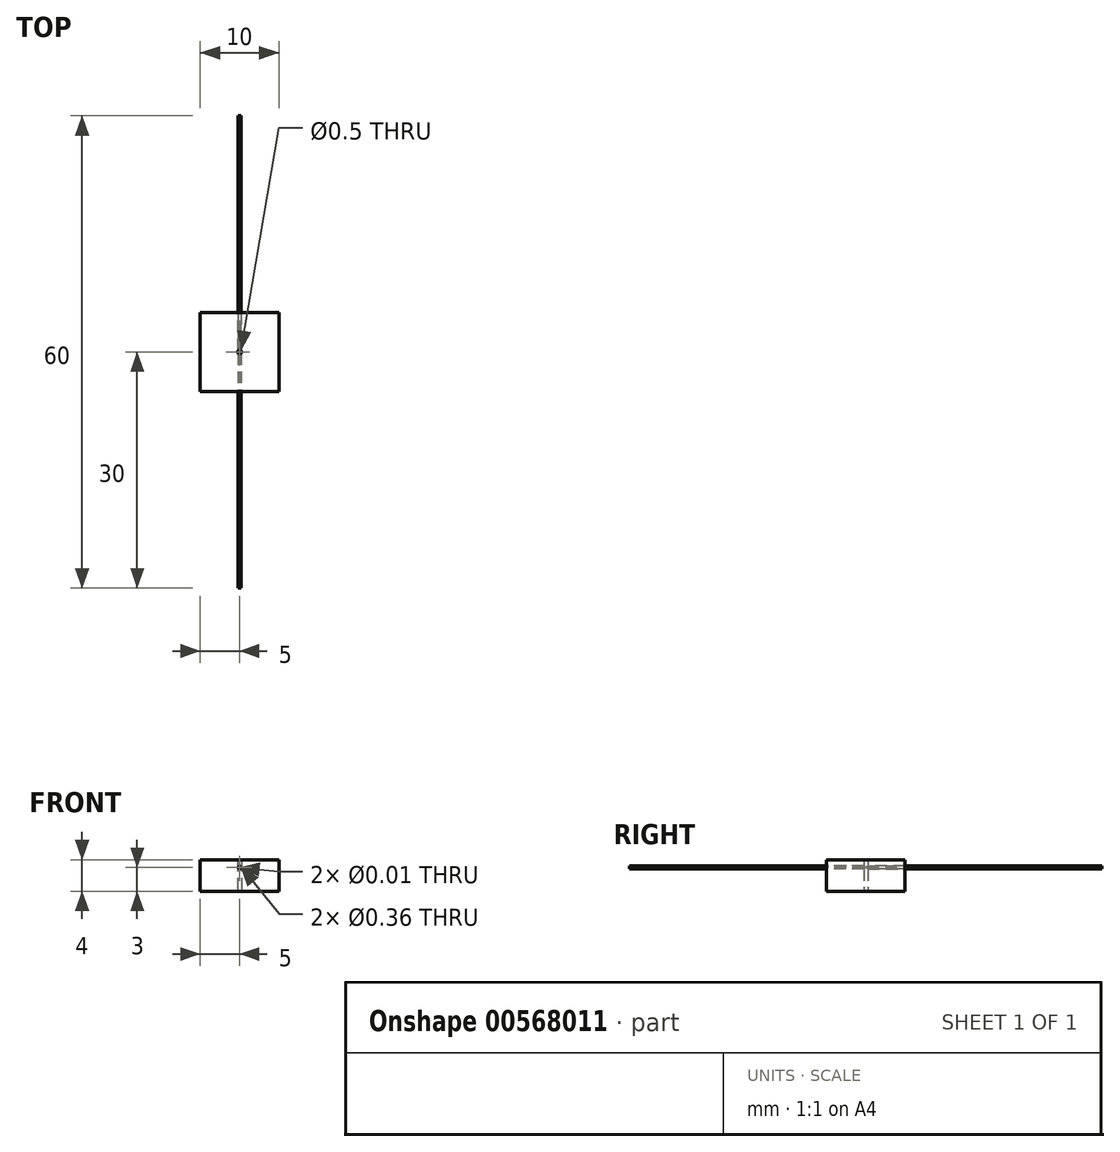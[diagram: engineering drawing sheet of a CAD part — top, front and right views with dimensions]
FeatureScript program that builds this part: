
annotation { "Feature Type Name" : "Feature", "Feature Type Description" : "" }
export const myFeature = defineFeature(function(context is Context, id is Id, definition is map)
    precondition{}
    {
        {
            var Q0;
            Q0=qCreatedBy(makeId("Top.planeOp"),FACE);
            var sketch = newSketch(context, id + "F0", { "sketchPlane" : qUnion([Q0])});
            skCircle(sketch, "E0", {"center": v(0, 0) * mm, "radius": 0.25 * mm});
            skLineSegment(sketch, "E1.bottom", {"start": v(5, 5) * mm, "end": v(-5, 5) * mm});
            skLineSegment(sketch, "E1.top", {"start": v(5, -5) * mm, "end": v(-5, -5) * mm});
            skLineSegment(sketch, "E1.left", {"start": v(5, 5) * mm, "end": v(5, -5) * mm});
            skLineSegment(sketch, "E1.right", {"start": v(-5, 5) * mm, "end": v(-5, -5) * mm});
            skSolve(sketch);
        }
        {
            var Q0;
            Q0 = qSketchRegion(id + "F0", true);
            extrude(context, id + "F1", {"entities" : qUnion([Q0]), "depth" : 4 * mm, "offsetDistance" : 25 * mm});
        }
        {
            var Q0;
            Q0=makeQuery(id+"F1.opExtrude","SWEPT_FACE",FACE,{"disambiguationData":[OSD([sQuery(id+"F0.wireOp",EDGE,"E1.top")])]});
            var sketch = newSketch(context, id + "F2", { "sketchPlane" : qUnion([Q0])});
            skLineSegment(sketch, "E2", {"start": v(0, 4) * mm, "end": v(0, 3) * mm, "construction": true});
            skPoint(sketch, "E2.endSnap0", {"position": v(0, 4) * mm});
            skCircle(sketch, "E3", {"center": v(0, 3) * mm, "radius": 0.18 * mm});
            skSolve(sketch);
        }
        {
            var Q0;
            Q0 = qSketchRegion(id + "F2", true);
            extrude(context, id + "F3", {"entities" : qUnion([Q0]), "operationType" : NewBodyOperationType.REMOVE, "endBound" : BoundingType.THROUGH_ALL, "oppositeDirection" : true, "depth" : 5 * mm, "offsetDistance" : 25 * mm});
        }
        {
            var Q0;
            Q0=makeQuery(id+"F1.opExtrude","SWEPT_FACE",FACE,{"disambiguationData":[OSD([sQuery(id+"F0.wireOp",EDGE,"E1.top")])]});
            var sketch = newSketch(context, id + "F4", { "sketchPlane" : qUnion([Q0])});
            skCircle(sketch, "E4.0", {"center": v(0, 3) * mm, "radius": 0.18 * mm});
            skCircle(sketch, "E5", {"center": v(0, 3) * mm, "radius": 0 * mm});
            skSolve(sketch);
        }
        {
            var Q0;
            Q0 = qSketchRegion(id + "F4", true);
            extrude(context, id + "F5", {"entities" : qUnion([Q0]), "oppositeDirection" : true, "depth" : 4.83 * mm, "offsetDistance" : 25 * mm, "hasSecondDirection" : true, "secondDirectionOppositeDirection" : false, "secondDirectionDepth" : 25 * mm});
        }
        {
            var Q0;
            Q0=makeQuery(id+"F1.opExtrude","SWEPT_FACE",FACE,{"disambiguationData":[OSD([sQuery(id+"F0.wireOp",EDGE,"E1.bottom")])]});
            var sketch = newSketch(context, id + "F6", { "sketchPlane" : qUnion([Q0])});
            skCircle(sketch, "E6.0", {"center": v(0, 3) * mm, "radius": 0.18 * mm});
            skCircle(sketch, "E7", {"center": v(0, 3) * mm, "radius": 0 * mm});
            skSolve(sketch);
        }
        {
            var Q0;
            Q0 = qSketchRegion(id + "F6", true);
            extrude(context, id + "F7", {"entities" : qUnion([Q0]), "oppositeDirection" : true, "depth" : 4.83 * mm, "offsetDistance" : 25 * mm, "hasSecondDirection" : true, "secondDirectionOppositeDirection" : false, "secondDirectionDepth" : 25 * mm});
        }
        {
            var Q0;
            Q0=qCreatedBy(makeId("Top.planeOp"),FACE);
            var sketch = newSketch(context, id + "F8", { "sketchPlane" : qUnion([Q0])});
            skCircle(sketch, "E8.0", {"center": v(0, 0) * mm, "radius": 0.25 * mm});
            skSolve(sketch);
        }
        {
            var Q0;
            Q0 = qSketchRegion(id + "F8", true);
            extrude(context, id + "F9", {"entities" : qUnion([Q0]), "depth" : 3 * mm, "offsetDistance" : 25 * mm});
        }
        {
            var Q0;
            Q0=makeQuery(id+"F1.opExtrude","SWEPT_BODY",BODY,{"disambiguationData":[OSD([sQuery(id+"F0.wireOp",EDGE,"E0"),sQuery(id+"F0.wireOp",EDGE,"E1.bottom"),sQuery(id+"F0.wireOp",EDGE,"E1.top"),sQuery(id+"F0.wireOp",EDGE,"E1.left"),sQuery(id+"F0.wireOp",EDGE,"E1.right")])]});
            var Q1;
            Q1=makeQuery(id+"F5.opExtrude","SWEPT_BODY",BODY,{"disambiguationData":[OSD([sQuery(id+"F4.wireOp",EDGE,"E4.0"),sQuery(id+"F4.wireOp",EDGE,"E5")])]});
            var Q2;
            Q2=makeQuery(id+"F7.opExtrude","SWEPT_BODY",BODY,{"disambiguationData":[OSD([sQuery(id+"F6.wireOp",EDGE,"E6.0"),sQuery(id+"F6.wireOp",EDGE,"E7")])]});
            var Q3;
            Q3=makeQuery(id+"F9.opExtrude","SWEPT_BODY",BODY,{"disambiguationData":[OSD([sQuery(id+"F8.wireOp",EDGE,"E8.0")])]});
            booleanBodies(context, id + "F10", {"operationType" : BooleanOperationType.SUBTRACTION, "tools" : qUnion([Q0, Q1, Q2]), "targets" : qUnion([Q3]), "keepTools" : true});
        }
        {
            var Q0;
            Q0=makeQuery(id+"F9.opExtrude","CAP_FACE",FACE,{"disambiguationData":[OSD([sQuery(id+"F8.wireOp",EDGE,"E8.0")])],"isStart":true});
            var sketch = newSketch(context, id + "F11", { "sketchPlane" : qUnion([Q0])});
            skCircle(sketch, "E9.0", {"center": v(0, 0) * mm, "radius": 0.25 * mm});
            skSolve(sketch);
        }
        {
            var Q0;
            Q0 = qSketchRegion(id + "F11", true);
            extrude(context, id + "F12", {"entities" : qUnion([Q0]), "operationType" : NewBodyOperationType.REMOVE, "oppositeDirection" : true, "depth" : 2.94 * mm, "offsetDistance" : 25 * mm});
        }
    });
